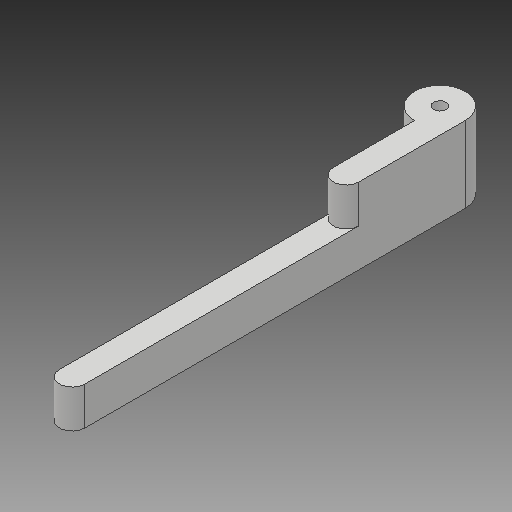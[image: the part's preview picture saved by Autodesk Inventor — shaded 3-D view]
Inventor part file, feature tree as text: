
AUTODESK INVENTOR PART (.ipt)
format: ipt  version: 2017 (Build 210142000, 142)  size: 119,808 bytes
history: native  units: mm
features: fillet x3, sketch x3, extrude x2, hole x1
ambient origin geometry x8: Origin, YZ Plane, XZ Plane, XY Plane, X Axis, Y Axis, Z Axis, Center Point
bodies: Solid1 (feature_tree)
feature tree (9):
  extrude  "Soporte Hoja"  Depth=3.0mm
  fillet  "Cabeza"  Radius=2.0mm
  fillet  "Agarre Hoja"  Radius=3.0mm
  hole  "Eje"  [1 undecoded]
  extrude  "Soporte Deslizador"  Depth=1.0mm
  fillet  "Agarre Deslizador"  Radius=3.0mm
  sketch  "Sketch1"  dims[d1=4.0mm d3=29.0mm d4=2.0mm d5=3.0mm d6=0.0mm]
  sketch  "Sketch2"  dims[d7=2.0mm d8=1.0mm]
  sketch  "Sketch3"  dims[d9=1.0mm d10=1.0mm d11=6.0mm d12=4.0mm d13=2.0mm d14=90.0deg d15=8.0mm d16=20.594885mm d17=11.4mm d18=3.0mm d19=0.0mm d20=1.0mm]
note: 1 required parameter value undecoded (feature->parameter linkage not recoverable at this tier; creation-order binding heuristic only, values carry confidence <= 0.55)
